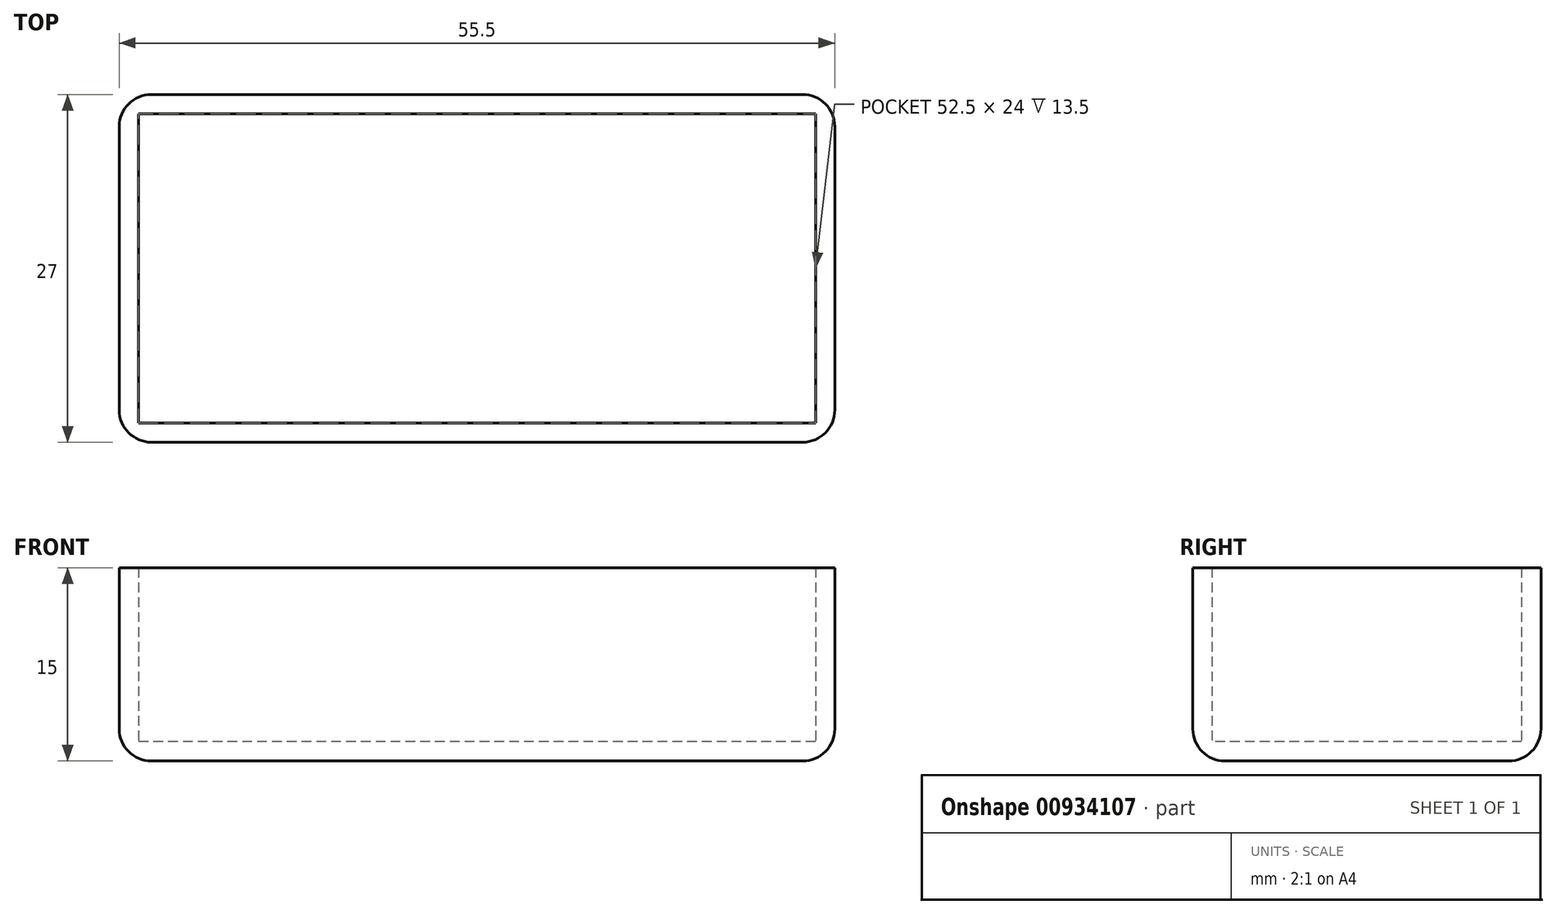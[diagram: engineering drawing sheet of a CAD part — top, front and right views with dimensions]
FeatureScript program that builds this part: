
annotation { "Feature Type Name" : "Feature", "Feature Type Description" : "" }
export const myFeature = defineFeature(function(context is Context, id is Id, definition is map)
    precondition{}
    {
        {
            var Q0;
            Q0=qCreatedBy(makeId("Top.planeOp"),FACE);
            var sketch = newSketch(context, id + "F0", { "sketchPlane" : qUnion([Q0])});
            skLineSegment(sketch, "E0.bottom", {"start": v(27.75, 13.5) * mm, "end": v(-27.75, 13.5) * mm});
            skLineSegment(sketch, "E0.top", {"start": v(27.75, -13.5) * mm, "end": v(-27.75, -13.5) * mm});
            skLineSegment(sketch, "E0.left", {"start": v(27.75, 13.5) * mm, "end": v(27.75, -13.5) * mm});
            skLineSegment(sketch, "E0.right", {"start": v(-27.75, 13.5) * mm, "end": v(-27.75, -13.5) * mm});
            skPoint(sketch, "E0.middle", {"position": v(0, 0) * mm});
            skSolve(sketch);
        }
        {
            var Q0;
            Q0=makeQuery(id+"F0.imprint","IMPRINT",FACE,{"disambiguationData":[TD([[makeQuery(id+"F0.imprint","IMPRINT",EDGE,{"derivedFrom":sQuery(id+"F0.wireOp",EDGE,"E0.bottom")}),1.0]])]});
            extrude(context, id + "F1", {"entities" : qUnion([Q0]), "depth" : 15 * mm, "offsetDistance" : 25 * mm});
        }
        {
            var Q0;
            Q0=makeQuery(id+"F1.opExtrude","CAP_FACE",FACE,{"disambiguationData":[OSD([sQuery(id+"F0.wireOp",EDGE,"E0.bottom"),sQuery(id+"F0.wireOp",EDGE,"E0.top"),sQuery(id+"F0.wireOp",EDGE,"E0.left"),sQuery(id+"F0.wireOp",EDGE,"E0.right")])],"isStart":false});
            shell(context, id + "F2", {"entities" : qUnion([Q0]), "thickness" : 1.5 * mm});
        }
        {
            var Q0;
            Q0=makeQuery(id+"F1.opExtrude","SWEPT_EDGE",EDGE,{"disambiguationData":[OSD([sQuery(id+"F0.wireOp",EDGE,"E0.bottom"),sQuery(id+"F0.wireOp",EDGE,"E0.left")])]});
            var Q1;
            Q1=makeQuery(id+"F1.opExtrude","SWEPT_EDGE",EDGE,{"disambiguationData":[OSD([sQuery(id+"F0.wireOp",EDGE,"E0.bottom"),sQuery(id+"F0.wireOp",EDGE,"E0.right")])]});
            var Q2;
            Q2=makeQuery(id+"F1.opExtrude","SWEPT_EDGE",EDGE,{"disambiguationData":[OSD([sQuery(id+"F0.wireOp",EDGE,"E0.top"),sQuery(id+"F0.wireOp",EDGE,"E0.left")])]});
            var Q3;
            Q3=makeQuery(id+"F1.opExtrude","SWEPT_EDGE",EDGE,{"disambiguationData":[OSD([sQuery(id+"F0.wireOp",EDGE,"E0.top"),sQuery(id+"F0.wireOp",EDGE,"E0.right")])]});
            fillet(context, id + "F3", {"entities" : qUnion([Q0, Q1, Q2, Q3]), "radius" : 2.5 * mm, "tangentPropagation" : true, "allowEdgeOverflow" : false});
        }
        {
            var Q0;
            Q0=makeQuery(id+"F1.opExtrude","CAP_FACE",FACE,{"disambiguationData":[OSD([sQuery(id+"F0.wireOp",EDGE,"E0.bottom"),sQuery(id+"F0.wireOp",EDGE,"E0.top"),sQuery(id+"F0.wireOp",EDGE,"E0.left"),sQuery(id+"F0.wireOp",EDGE,"E0.right")])],"isStart":true});
            fillet(context, id + "F4", {"entities" : qUnion([Q0]), "radius" : 2.5 * mm, "tangentPropagation" : true, "allowEdgeOverflow" : false});
        }
    });
